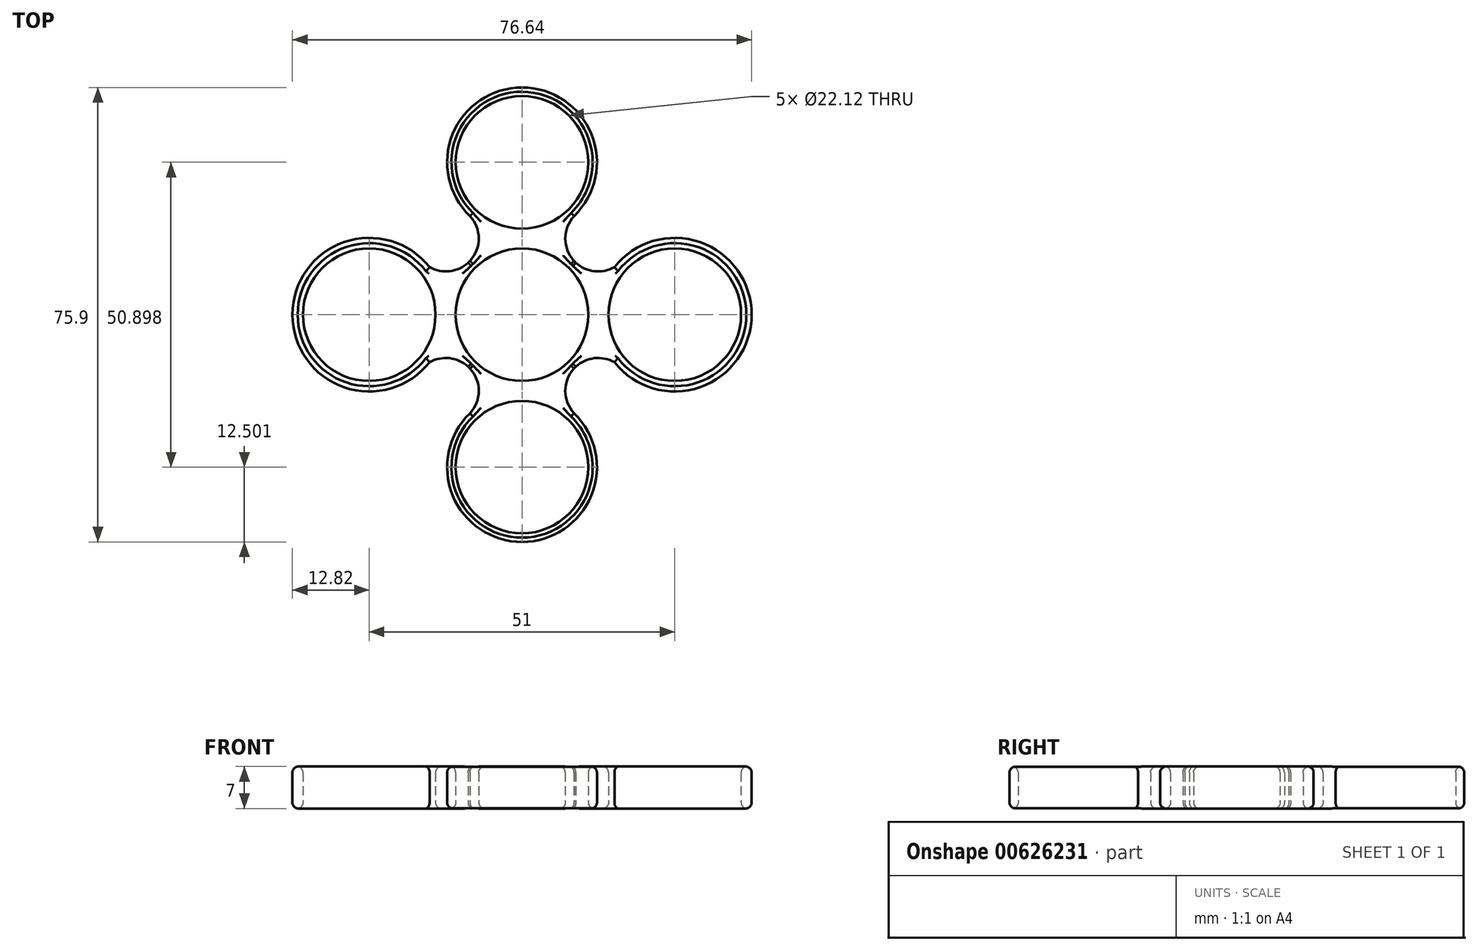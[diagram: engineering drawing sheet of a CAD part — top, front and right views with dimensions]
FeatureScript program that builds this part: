
annotation { "Feature Type Name" : "Feature", "Feature Type Description" : "" }
export const myFeature = defineFeature(function(context is Context, id is Id, definition is map)
    precondition{}
    {
        {
            var Q0;
            Q0=qCreatedBy(makeId("Top.planeOp"),FACE);
            var sketch = newSketch(context, id + "F0", { "sketchPlane" : qUnion([Q0])});
            skCircle(sketch, "E0", {"center": v(0, 0) * mm, "radius": 11.06 * mm});
            skCircle(sketch, "E1", {"center": v(0, 0) * mm, "radius": 12.5 * mm});
            skLineSegment(sketch, "E2.MirrorCS", {"start": v(0, -25.45) * mm, "end": v(0, -25.5) * mm});
            skCircle(sketch, "E3", {"center": v(0, 25.45) * mm, "radius": 11.06 * mm});
            skCircle(sketch, "E4", {"center": v(0, 25.45) * mm, "radius": 12.5 * mm});
            skLineSegment(sketch, "E5", {"start": v(0, 0) * mm, "end": v(-2.45, 0) * mm, "construction": true});
            skLineSegment(sketch, "E6", {"start": v(2.82, 0) * mm, "end": v(0, 0) * mm, "construction": true});
            skLineSegment(sketch, "E7", {"start": v(0, 2.88) * mm, "end": v(0, -2.34) * mm, "construction": true});
            skCircle(sketch, "E8.MirrorC", {"center": v(0, -25.45) * mm, "radius": 11.06 * mm});
            skCircle(sketch, "E9.MirrorC", {"center": v(0, -25.45) * mm, "radius": 12.5 * mm});
            skCircle(sketch, "E10", {"center": v(25.5, 0) * mm, "radius": 12.82 * mm});
            skCircle(sketch, "E11", {"center": v(25.5, 0) * mm, "radius": 11.06 * mm});
            skCircle(sketch, "E12.MirrorC", {"center": v(-25.5, 0) * mm, "radius": 11.06 * mm});
            skCircle(sketch, "E13.MirrorC", {"center": v(-25.5, 0) * mm, "radius": 12.82 * mm});
            skLineSegment(sketch, "E14", {"start": v(0, 0) * mm, "end": v(25.45, 25.45) * mm, "construction": true});
            skArc(sketch, "E15", {"start": v(8.7, 16.48) * mm, "mid": v(8.4, 9.32) * mm, "end": v(15.43, 7.93) * mm});
            skArc(sketch, "E16.MirrorCS", {"start": v(8.7, -16.48) * mm, "mid": v(8.4, -9.32) * mm, "end": v(15.43, -7.93) * mm});
            skArc(sketch, "E17.MirrorCS", {"start": v(-8.7, -16.48) * mm, "mid": v(-8.4, -9.32) * mm, "end": v(-15.43, -7.93) * mm});
            skArc(sketch, "E18.MirrorCS", {"start": v(-8.7, 16.48) * mm, "mid": v(-8.4, 9.32) * mm, "end": v(-15.43, 7.93) * mm});
            skPoint(sketch, "E19.start.orphan", {"position": v(0, 12.5) * mm});
            skPoint(sketch, "E20.start.orphan", {"position": v(12.5, 0) * mm});
            skSolve(sketch);
        }
        {
            var Q0;
            Q0 = qSketchRegion(id + "F0", true);
            extrude(context, id + "F1", {"entities" : qUnion([Q0]), "depth" : 7 * mm, "offsetDistance" : 25 * mm});
        }
        {
            var Q0;
            Q0=makeQuery(id+"F1.opExtrude","CAP_EDGE",EDGE,{"disambiguationData":[OSD([sQuery(id+"F0.wireOp",EDGE,"E13.MirrorC")])],"isStart":false});
            var Q1;
            {var subQ0=sQuery(id+"F0.wireOp",EDGE,"E17.MirrorCS");Q1=makeQuery(id+"F1.opExtrude","CAP_EDGE",EDGE,{"disambiguationData":[OSD([subQ0]),TDD([makeQuery(id+"F0.imprint","IMPRINT",EDGE,{"disambiguationData":[TD([[makeQuery(id+"F0.imprint","INTERSECT",VERTEX,{"derivedFrom":[sQuery(id+"F0.wireOp",EDGE,"E13.MirrorC"),subQ0]}),1.0]])],"derivedFrom":subQ0})])],"isStart":false});}
            var Q2;
            {var subQ0=sQuery(id+"F0.wireOp",EDGE,"E17.MirrorCS");Q2=makeQuery(id+"F1.opExtrude","CAP_EDGE",EDGE,{"disambiguationData":[OSD([subQ0]),TDD([makeQuery(id+"F0.imprint","IMPRINT",EDGE,{"disambiguationData":[TD([[makeQuery(id+"F0.imprint","INTERSECT",VERTEX,{"derivedFrom":[sQuery(id+"F0.wireOp",EDGE,"E9.MirrorC"),subQ0]}),-1.0]])],"derivedFrom":subQ0})])],"isStart":false});}
            var Q3;
            {var subQ0=sQuery(id+"F0.wireOp",EDGE,"E17.MirrorCS");var subQ1=sQuery(id+"F0.wireOp",EDGE,"E1");Q3=makeQuery(id+"F1.opExtrude","CAP_EDGE",EDGE,{"disambiguationData":[OSD([subQ1]),TDD([makeQuery(id+"F0.imprint","IMPRINT",EDGE,{"disambiguationData":[TD([[makeQuery(id+"F0.imprint","INTERSECT",VERTEX,{"disambiguationData":[OD(0.0)],"derivedFrom":[subQ1,subQ0]}),-1.0]])],"derivedFrom":subQ1})])],"isStart":false});}
            var Q4;
            Q4=makeQuery(id+"F1.opExtrude","CAP_FACE",FACE,{"disambiguationData":[OSD([sQuery(id+"F0.wireOp",EDGE,"E1"),sQuery(id+"F0.wireOp",EDGE,"E0"),sQuery(id+"F0.wireOp",EDGE,"E4"),sQuery(id+"F0.wireOp",EDGE,"E3"),sQuery(id+"F0.wireOp",EDGE,"E8.MirrorC"),sQuery(id+"F0.wireOp",EDGE,"E9.MirrorC"),sQuery(id+"F0.wireOp",EDGE,"E10"),sQuery(id+"F0.wireOp",EDGE,"E11"),sQuery(id+"F0.wireOp",EDGE,"E12.MirrorC"),sQuery(id+"F0.wireOp",EDGE,"E13.MirrorC"),sQuery(id+"F0.wireOp",EDGE,"E15"),sQuery(id+"F0.wireOp",EDGE,"E16.MirrorCS"),sQuery(id+"F0.wireOp",EDGE,"E17.MirrorCS"),sQuery(id+"F0.wireOp",EDGE,"E18.MirrorCS")])],"isStart":false});
            var Q5;
            Q5=makeQuery(id+"F1.opExtrude","CAP_FACE",FACE,{"disambiguationData":[OSD([sQuery(id+"F0.wireOp",EDGE,"E1"),sQuery(id+"F0.wireOp",EDGE,"E0"),sQuery(id+"F0.wireOp",EDGE,"E4"),sQuery(id+"F0.wireOp",EDGE,"E3"),sQuery(id+"F0.wireOp",EDGE,"E8.MirrorC"),sQuery(id+"F0.wireOp",EDGE,"E9.MirrorC"),sQuery(id+"F0.wireOp",EDGE,"E10"),sQuery(id+"F0.wireOp",EDGE,"E11"),sQuery(id+"F0.wireOp",EDGE,"E12.MirrorC"),sQuery(id+"F0.wireOp",EDGE,"E13.MirrorC"),sQuery(id+"F0.wireOp",EDGE,"E15"),sQuery(id+"F0.wireOp",EDGE,"E16.MirrorCS"),sQuery(id+"F0.wireOp",EDGE,"E17.MirrorCS"),sQuery(id+"F0.wireOp",EDGE,"E18.MirrorCS")])],"isStart":true});
            fillet(context, id + "F2", {"entities" : qUnion([Q0, Q1, Q2, Q3, Q4, Q5]), "radius" : 1 * mm, "tangentPropagation" : true, "allowEdgeOverflow" : false});
        }
    });
